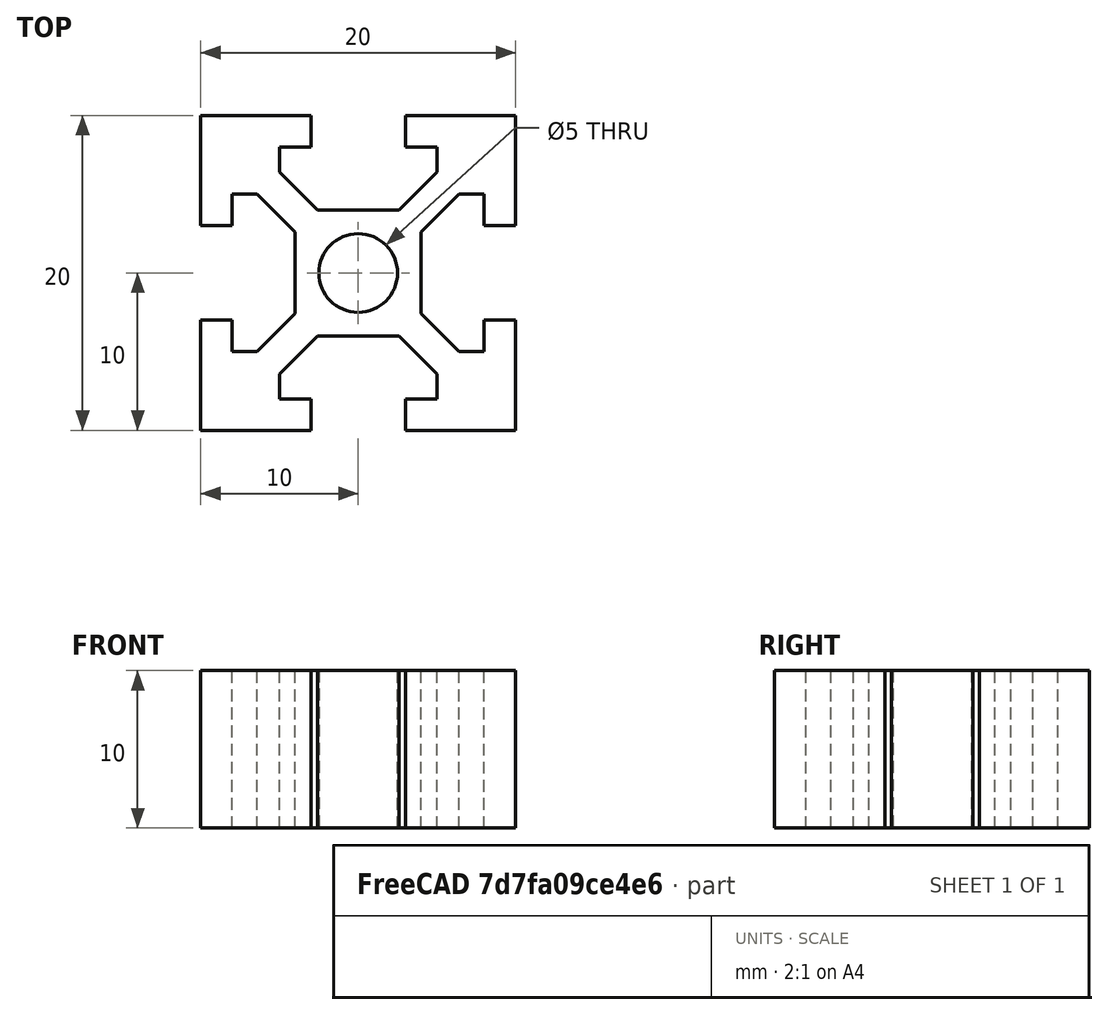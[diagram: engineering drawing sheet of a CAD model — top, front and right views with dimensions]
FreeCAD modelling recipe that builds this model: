
FCSTD DOCUMENT  (FreeCAD 0.19R24276 (Git))
Label: AL_profil_20
License: All rights reserved
LicenseURL: http://en.wikipedia.org/wiki/All_rights_reserved
objects: Sketcher::SketchObject×1, PartDesign::Pad×1, PartDesign::Body×1
note: 4 computed .brp shape members not serialized (recipe doc carries the construction recipe); baked Part::Feature solids carry a one-line shape summary decoded from their .brp

FEATURE [Sketcher::SketchObject] Sketch
  FullyConstrained = false
  MapMode = 5
  Support = -> [XY_Plane]
  sketch-geometry (106):
    g0: LineSegment StartX=10 StartY=10 StartZ=0 EndX=-10 EndY=10 EndZ=0
    g1: LineSegment StartX=-10 StartY=10 StartZ=0 EndX=-10 EndY=-10 EndZ=0
    g2: LineSegment StartX=-10 StartY=-10 StartZ=0 EndX=10 EndY=-10 EndZ=0
    g3: LineSegment StartX=10 StartY=-10 StartZ=0 EndX=10 EndY=10 EndZ=0
    g4: Circle CenterX=0 CenterY=0 CenterZ=0 NormalX=0 NormalY=0 NormalZ=1 AngleXU=0 Radius=14.1421
    g5: LineSegment StartX=4 StartY=4 StartZ=0 EndX=-4 EndY=4 EndZ=0
    g6: LineSegment StartX=-4 StartY=4 StartZ=0 EndX=-4 EndY=-4 EndZ=0
    g7: LineSegment StartX=-4 StartY=-4 StartZ=0 EndX=4 EndY=-4 EndZ=0
    g8: LineSegment StartX=4 StartY=-4 StartZ=0 EndX=4 EndY=4 EndZ=0
    g9: Circle CenterX=0 CenterY=0 CenterZ=0 NormalX=0 NormalY=0 NormalZ=1 AngleXU=0 Radius=5.65685
    g10: Circle CenterX=0 CenterY=0 CenterZ=0 NormalX=0 NormalY=0 NormalZ=1 AngleXU=0 Radius=2.5
    g11: LineSegment StartX=-10 StartY=-10 StartZ=0 EndX=-5 EndY=-10 EndZ=0
    g12: LineSegment StartX=-5 StartY=-10 StartZ=0 EndX=-5 EndY=-5 EndZ=0
    g13: LineSegment StartX=-5 StartY=-5 StartZ=0 EndX=-10 EndY=-5 EndZ=0
    g14: LineSegment StartX=-10 StartY=-5 StartZ=0 EndX=-10 EndY=-10 EndZ=0
    g15: LineSegment StartX=10 StartY=-10 StartZ=0 EndX=5 EndY=-10 EndZ=0
    g16: LineSegment StartX=5 StartY=-8 StartZ=0 EndX=5 EndY=-5 EndZ=0
    g17: LineSegment StartX=5 StartY=-5 StartZ=0 EndX=10 EndY=-5 EndZ=0
    g18: LineSegment StartX=10 StartY=-5 StartZ=0 EndX=10 EndY=-10 EndZ=0
    g19: LineSegment StartX=10 StartY=10 StartZ=0 EndX=5 EndY=10 EndZ=0
    g20: LineSegment StartX=5 StartY=10 StartZ=0 EndX=5 EndY=5 EndZ=0
    g21: LineSegment StartX=5 StartY=5 StartZ=0 EndX=10 EndY=5 EndZ=0
    g22: LineSegment StartX=10 StartY=5 StartZ=0 EndX=10 EndY=10 EndZ=0
    g23: LineSegment StartX=-10 StartY=10 StartZ=0 EndX=-5 EndY=10 EndZ=0
    g24: LineSegment StartX=-5 StartY=10 StartZ=0 EndX=-5 EndY=5 EndZ=0
    g25: LineSegment StartX=-5 StartY=5 StartZ=0 EndX=-10 EndY=5 EndZ=0
    g26: LineSegment StartX=-10 StartY=5 StartZ=0 EndX=-10 EndY=10 EndZ=0
    g27: LineSegment StartX=-6.41421 StartY=-5 StartZ=0 EndX=-4 EndY=-2.58579 EndZ=0
    g28: LineSegment StartX=-5 StartY=-6.41421 StartZ=0 EndX=-2.58579 EndY=-4 EndZ=0
    g29: LineSegment StartX=-5 StartY=-5 StartZ=0 EndX=-4 EndY=-4 EndZ=0
    g30: LineSegment StartX=-4 StartY=-4 StartZ=0 EndX=-5.70711 EndY=-5.70711 EndZ=0
    g31: LineSegment StartX=-6.41421 StartY=5 StartZ=0 EndX=-4 EndY=2.58579 EndZ=0
    g32: LineSegment StartX=-5 StartY=6.41421 StartZ=0 EndX=-2.58579 EndY=4 EndZ=0
    g33: LineSegment StartX=-5 StartY=5 StartZ=0 EndX=-4 EndY=4 EndZ=0
    g34: LineSegment StartX=-4 StartY=4 StartZ=0 EndX=-5.70711 EndY=5.70711 EndZ=0
    g35: LineSegment StartX=6.41421 StartY=-5 StartZ=0 EndX=4 EndY=-2.58579 EndZ=0
    g36: LineSegment StartX=5 StartY=-6.41421 StartZ=0 EndX=2.58579 EndY=-4 EndZ=0
    g37: LineSegment StartX=5 StartY=-5 StartZ=0 EndX=4 EndY=-4 EndZ=0
    g38: LineSegment StartX=4 StartY=-4 StartZ=0 EndX=5.70711 EndY=-5.70711 EndZ=0
    g39: LineSegment StartX=6.41421 StartY=5 StartZ=0 EndX=4 EndY=2.58579 EndZ=0
    g40: LineSegment StartX=5 StartY=6.41421 StartZ=0 EndX=2.58579 EndY=4 EndZ=0
    g41: LineSegment StartX=5 StartY=5 StartZ=0 EndX=4 EndY=4 EndZ=0
    g42: LineSegment StartX=4 StartY=4 StartZ=0 EndX=5.70711 EndY=5.70711 EndZ=0
    g43: LineSegment StartX=10 StartY=-10 StartZ=0 EndX=3 EndY=-10 EndZ=0
    g44: LineSegment StartX=3 StartY=-10 StartZ=0 EndX=3 EndY=-8 EndZ=0
    g45: LineSegment StartX=3 StartY=-8 StartZ=0 EndX=5 EndY=-8 EndZ=0
    g46: LineSegment StartX=10 StartY=-8 StartZ=0 EndX=10 EndY=-10 EndZ=0
    g47: LineSegment StartX=10 StartY=-3 StartZ=0 EndX=8 EndY=-3 EndZ=0
    g48: LineSegment StartX=8 StartY=-3 StartZ=0 EndX=8 EndY=-5 EndZ=0
    g49: LineSegment StartX=3 StartY=-10 StartZ=0 EndX=3 EndY=-8 EndZ=0
    g50: LineSegment StartX=3 StartY=-8 StartZ=0 EndX=5 EndY=-8 EndZ=0
    g51: LineSegment StartX=5 StartY=-8 StartZ=0 EndX=5 EndY=-6.41421 EndZ=0
    g52: LineSegment StartX=5 StartY=-6.41421 StartZ=0 EndX=2.58579 EndY=-4 EndZ=0
    g53: LineSegment StartX=4 StartY=-2.58579 StartZ=0 EndX=6.41421 EndY=-5 EndZ=0
    g54: LineSegment StartX=6.41421 StartY=-5 StartZ=0 EndX=8 EndY=-5 EndZ=0
    g55: LineSegment StartX=8 StartY=-5 StartZ=0 EndX=8 EndY=-3 EndZ=0
    g56: LineSegment StartX=8 StartY=-3 StartZ=0 EndX=10 EndY=-3 EndZ=0
    g57: LineSegment StartX=-2.58579 StartY=-4 StartZ=0 EndX=2.58579 EndY=-4 EndZ=0
    g58: LineSegment StartX=3 StartY=10 StartZ=0 EndX=3 EndY=8 EndZ=0
    g59: LineSegment StartX=3 StartY=8 StartZ=0 EndX=5 EndY=8 EndZ=0
    g60: LineSegment StartX=3 StartY=10 StartZ=0 EndX=3 EndY=8 EndZ=0
    g61: LineSegment StartX=3 StartY=8 StartZ=0 EndX=5 EndY=8 EndZ=0
    g62: LineSegment StartX=10 StartY=3 StartZ=0 EndX=8 EndY=3 EndZ=0
    g63: LineSegment StartX=8 StartY=3 StartZ=0 EndX=8 EndY=5 EndZ=0
    g64: LineSegment StartX=8 StartY=5 StartZ=0 EndX=8 EndY=3 EndZ=0
    g65: LineSegment StartX=8 StartY=3 StartZ=0 EndX=10 EndY=3 EndZ=0
    g66: LineSegment StartX=2.58579 StartY=4 StartZ=0 EndX=5 EndY=6.41421 EndZ=0
    g67: LineSegment StartX=5 StartY=6.41421 StartZ=0 EndX=5 EndY=8 EndZ=0
    g68: LineSegment StartX=-2.58579 StartY=4 StartZ=0 EndX=2.58579 EndY=4 EndZ=0
    g69: LineSegment StartX=4 StartY=2.58579 StartZ=0 EndX=6.41421 EndY=5 EndZ=0
    g70: LineSegment StartX=6.41421 StartY=5 StartZ=0 EndX=8 EndY=5 EndZ=0
    g71: LineSegment StartX=4 StartY=-2.58579 StartZ=0 EndX=4 EndY=2.58579 EndZ=0
    g72: LineSegment StartX=10 StartY=3 StartZ=0 EndX=10 EndY=10 EndZ=0
    g73: LineSegment StartX=10 StartY=-10 StartZ=0 EndX=10 EndY=-3 EndZ=0
    g74: LineSegment StartX=-3 StartY=-10 StartZ=0 EndX=-3 EndY=-8 EndZ=0
    g75: LineSegment StartX=-3 StartY=-8 StartZ=0 EndX=-5 EndY=-8 EndZ=0
    g76: LineSegment StartX=-3 StartY=-10 StartZ=0 EndX=-3 EndY=-8 EndZ=0
    g77: LineSegment StartX=-3 StartY=-8 StartZ=0 EndX=-5 EndY=-8 EndZ=0
    g78: LineSegment StartX=-5 StartY=-8 StartZ=0 EndX=-5 EndY=-6.41421 EndZ=0
    g79: LineSegment StartX=-10 StartY=-3 StartZ=0 EndX=-8 EndY=-3 EndZ=0
    g80: LineSegment StartX=-8 StartY=-3 StartZ=0 EndX=-8 EndY=-5 EndZ=0
    g81: LineSegment StartX=-6.41421 StartY=-5 StartZ=0 EndX=-8 EndY=-5 EndZ=0
    g82: LineSegment StartX=-8 StartY=-5 StartZ=0 EndX=-8 EndY=-3 EndZ=0
    g83: LineSegment StartX=-8 StartY=-3 StartZ=0 EndX=-10 EndY=-3 EndZ=0
    g84: LineSegment StartX=-10 StartY=10 StartZ=0 EndX=10 EndY=10 EndZ=0
    g85: LineSegment StartX=-6.41421 StartY=-5 StartZ=0 EndX=-4 EndY=-2.58579 EndZ=0
    g86: LineSegment StartX=-4 StartY=2.58579 StartZ=0 EndX=-4 EndY=-2.58579 EndZ=0
    g87: LineSegment StartX=-5 StartY=-6.41421 StartZ=0 EndX=-2.58579 EndY=-4 EndZ=0
    g88: LineSegment StartX=3 StartY=-10 StartZ=0 EndX=10 EndY=-10 EndZ=0
    g89: LineSegment StartX=-3 StartY=-10 StartZ=0 EndX=-10 EndY=-10 EndZ=0
    g90: LineSegment StartX=-10 StartY=3 StartZ=0 EndX=-8 EndY=3 EndZ=0
    g91: LineSegment StartX=-8 StartY=3 StartZ=0 EndX=-8 EndY=5 EndZ=0
    g92: LineSegment StartX=-8 StartY=5 StartZ=0 EndX=-8 EndY=3 EndZ=0
    g93: LineSegment StartX=-8 StartY=3 StartZ=0 EndX=-10 EndY=3 EndZ=0
    g94: LineSegment StartX=-3 StartY=10 StartZ=0 EndX=-3 EndY=8 EndZ=0
    g95: LineSegment StartX=-3 StartY=8 StartZ=0 EndX=-5 EndY=8 EndZ=0
    g96: LineSegment StartX=-3 StartY=10 StartZ=0 EndX=-3 EndY=8 EndZ=0
    g97: LineSegment StartX=-3 StartY=8 StartZ=0 EndX=-5 EndY=8 EndZ=0
    g98: LineSegment StartX=-5 StartY=8 StartZ=0 EndX=-5 EndY=6.41421 EndZ=0
    g99: LineSegment StartX=-6.41421 StartY=5 StartZ=0 EndX=-8 EndY=5 EndZ=0
    g100: LineSegment StartX=-5 StartY=6.41421 StartZ=0 EndX=-2.58579 EndY=4 EndZ=0
    g101: LineSegment StartX=-6.41421 StartY=5 StartZ=0 EndX=-4 EndY=2.58579 EndZ=0
    g102: LineSegment StartX=-10 StartY=-3 StartZ=0 EndX=-10 EndY=-10 EndZ=0
    g103: LineSegment StartX=-10 StartY=3 StartZ=0 EndX=-10 EndY=10 EndZ=0
    g104: LineSegment StartX=-10 StartY=10 StartZ=0 EndX=-3 EndY=10 EndZ=0
    g105: LineSegment StartX=3 StartY=10 StartZ=0 EndX=10 EndY=10 EndZ=0
  constraints (271):
    c: Coincident(g0,g1)
    c: Coincident(g1,g2)
    c: Coincident(g2,g3)
    c: Coincident(g3,g0)
    c: Equal(g0,g1)
    c: Equal(g0,g2)
    c: Equal(g0,g3)
    c: PointOnObject(g0,g4)
    c: PointOnObject(g1,g4)
    c: PointOnObject(g2,g4)
    c: PointOnObject(g3,g4)
    c: Coincident(g4,g-1)
    c: Horizontal(g0)
    c: Coincident(g5,g6)
    c: Coincident(g6,g7)
    c: Coincident(g7,g8)
    c: Coincident(g8,g5)
    c: Equal(g5,g6)
    c: Equal(g5,g7)
    c: Equal(g5,g8)
    c: PointOnObject(g5,g9)
    c: PointOnObject(g6,g9)
    c: PointOnObject(g7,g9)
    c: PointOnObject(g8,g9)
    c: Coincident(g9,g-1)
    c: Horizontal(g5)
    c: DistanceX(g5,g5) = 8
    c: Diameter(g10) = 5
    c: DistanceX(g2,g2) = 20
    c: Coincident(g10,g-1)
    c: Coincident(g11,g12)
    c: Coincident(g12,g13)
    c: Coincident(g13,g14)
    c: Coincident(g14,g11)
    c: Horizontal(g11)
    c: Horizontal(g13)
    c: Vertical(g12)
    c: Vertical(g14)
    c: Coincident(g11,g1)
    c: Coincident(g16,g17)
    c: Coincident(g17,g18)
    c: Coincident(g18,g15)
    c: Horizontal(g15)
    c: Horizontal(g17)
    c: Vertical(g16)
    c: Vertical(g18)
    c: Coincident(g15,g2)
    c: Coincident(g19,g20)
    c: Coincident(g20,g21)
    c: Coincident(g21,g22)
    c: Coincident(g22,g19)
    c: Horizontal(g19)
    c: Horizontal(g21)
    c: Vertical(g20)
    c: Vertical(g22)
    c: Coincident(g19,g0)
    c: Coincident(g23,g24)
    c: Coincident(g24,g25)
    c: Coincident(g25,g26)
    c: Coincident(g26,g23)
    c: Horizontal(g23)
    c: Horizontal(g25)
    c: Vertical(g24)
    c: Vertical(g26)
    c: Coincident(g23,g0)
    c: DistanceX(g1,g11) = 5
    c: Equal(g12,g13)
    c: Equal(g13,g17)
    c: Equal(g25,g13)
    c: Equal(g13,g21)
    c: Equal(g24,g20)
    c: Equal(g20,g12)
    c: Parallel(g27,g28)
    c: Coincident(g29,g12)
    c: Coincident(g29,g6)
    c: Parallel(g27,g29)
    c: Coincident(g30,g6)
    c: Parallel(g29,g30)
    c: PointOnObject(g28,g12)
    c: PointOnObject(g27,g13)
    c: Distance(g28,g27) = 2
    c: PointOnObject(g27,g6)
    c: PointOnObject(g28,g7)
    c: Symmetric(g27,g28,g30)
    c: Parallel(g31,g32)
    c: Parallel(g31,g33)
    c: Parallel(g33,g34)
    c: Coincident(g33,g34)
    c: Coincident(g33,g5)
    c: Coincident(g33,g24)
    c: PointOnObject(g31,g25)
    c: PointOnObject(g32,g24)
    c: PointOnObject(g32,g5)
    c: PointOnObject(g31,g6)
    c: Symmetric(g31,g32,g34)
    c: Distance(g31,g32) = 2
    c: Parallel(g35,g36)
    c: Parallel(g35,g37)
    c: Parallel(g37,g38)
    c: Parallel(g39,g40)
    c: Parallel(g39,g41)
    c: Parallel(g41,g42)
    c: Coincident(g41,g42)
    c: Coincident(g41,g5)
    c: PointOnObject(g40,g5)
    c: PointOnObject(g39,g8)
    c: PointOnObject(g39,g21)
    c: PointOnObject(g40,g20)
    c: Coincident(g20,g41)
    c: Distance(g40,g39) = 2
    c: Symmetric(g40,g39,g42)
    c: PointOnObject(g35,g8)
    c: PointOnObject(g35,g17)
    c: PointOnObject(g36,g16)
    c: PointOnObject(g36,g7)
    c: Coincident(g38,g37)
    c: Coincident(g38,g7)
    c: Coincident(g37,g16)
    c: Symmetric(g36,g35,g38)
    c: Distance(g36,g35) = 2
    c: Coincident(g43,g44)
    c: Coincident(g44,g45)
    c: Coincident(g46,g43)
    c: Horizontal(g43)
    c: Horizontal(g45)
    c: Vertical(g44)
    c: Vertical(g46)
    c: Coincident(g43,g2)
    c: DistanceX(g43,g2) = 7
    c: DistanceY(g2,g46) = 2
    c: Coincident(g45,g16)
    c: Coincident(g47,g48)
    c: Equal(g44,g47)
    c: Vertical(g48)
    c: Horizontal(g47)
    c: Vertical(g47,g2)
    c: Horizontal(g17,g13)
    c: PointOnObject(g48,g17)
    c: DistanceY(g2,g47) = 7
    c: DistanceX(g47,g47) = 2
    c: Coincident(g49,g43)
    c: Coincident(g50,g44)
    c: Coincident(g51,g50)
    c: Coincident(g52,g51)
    c: Coincident(g53,g35)
    c: Coincident(g54,g53)
    c: Coincident(g55,g48)
    c: Coincident(g56,g55)
    c: Coincident(g49,g50)
    c: Coincident(g50,g16)
    c: Coincident(g51,g36)
    c: Coincident(g52,g36)
    c: Coincident(g53,g35)
    c: Coincident(g54,g55)
    c: Coincident(g55,g47)
    c: Coincident(g56,g47)
    c: Coincident(g57,g28)
    c: Coincident(g57,g52)
    c: Coincident(g58,g59)
    c: Horizontal(g59)
    c: Vertical(g58)
    c: Coincident(g62,g63)
    c: Equal(g58,g62)
    c: Vertical(g63)
    c: Horizontal(g62)
    c: Coincident(g61,g58)
    c: Coincident(g64,g63)
    c: Coincident(g65,g64)
    c: Coincident(g60,g61)
    c: Coincident(g64,g62)
    c: Coincident(g65,g62)
    c: Equal(g56,g65)
    c: Vertical(g65,g56)
    c: Equal(g55,g64)
    c: Horizontal(g64,g21)
    c: Equal(g61,g64)
    c: Horizontal(g60,g19)
    c: Coincident(g60,g58)
    c: Coincident(g61,g59)
    c: Vertical(g61,g19)
    c: Coincident(g66,g40)
    c: Coincident(g67,g66)
    c: Coincident(g67,g61)
    c: Coincident(g66,g40)
    c: Coincident(g68,g32)
    c: Coincident(g68,g66)
    c: Coincident(g69,g39)
    c: Coincident(g70,g69)
    c: Coincident(g69,g39)
    c: Coincident(g70,g64)
    c: Coincident(g71,g53)
    c: Coincident(g71,g69)
    c: Coincident(g72,g65)
    c: Coincident(g72,g0)
    c: Coincident(g73,g2)
    c: Coincident(g73,g56)
    c: Horizontal(g84)
    c: Coincident(g74,g75)
    c: Horizontal(g75)
    c: Vertical(g74)
    c: Coincident(g79,g80)
    c: Equal(g74,g79)
    c: Vertical(g80)
    c: Horizontal(g79)
    c: Coincident(g77,g74)
    c: Coincident(g78,g77)
    c: Coincident(g82,g80)
    c: Coincident(g83,g82)
    c: Coincident(g76,g77)
    c: Coincident(g81,g82)
    c: Coincident(g82,g79)
    c: Coincident(g83,g79)
    c: Horizontal(g76,g49)
    c: Horizontal(g76,g49)
    c: Vertical(g78)
    c: Coincident(g77,g75)
    c: Coincident(g78,g28)
    c: Equal(g77,g50)
    c: Vertical(g83,g1)
    c: Coincident(g74,g76)
    c: Equal(g82,g77)
    c: Horizontal(g81)
    c: Coincident(g81,g27)
    c: Coincident(g85,g81)
    c: Coincident(g85,g27)
    c: Coincident(g86,g31)
    c: Coincident(g86,g85)
    c: Coincident(g87,g78)
    c: Coincident(g87,g57)
    c: Coincident(g88,g49)
    c: Coincident(g89,g76)
    c: Coincident(g1,g89)
    c: Coincident(g88,g73)
    c: Coincident(g94,g95)
    c: Horizontal(g95)
    c: Vertical(g94)
    c: Coincident(g90,g91)
    c: Equal(g94,g90)
    c: Vertical(g91)
    c: Horizontal(g90)
    c: Coincident(g97,g94)
    c: Coincident(g98,g97)
    c: Coincident(g92,g91)
    c: Coincident(g93,g92)
    c: Coincident(g96,g97)
    c: Coincident(g99,g92)
    c: Coincident(g92,g90)
    c: Coincident(g93,g90)
    c: Vertical(g98)
    c: Coincident(g97,g95)
    c: Coincident(g94,g96)
    c: Equal(g92,g97)
    c: Horizontal(g99)
    c: Horizontal(g96,g23)
    c: Equal(g97,g61)
    c: Horizontal(g60,g96)
    c: Coincident(g98,g32)
    c: Coincident(g100,g98)
    c: Coincident(g68,g100)
    c: Coincident(g99,g31)
    c: Vertical(g92,g82)
    c: Coincident(g101,g99)
    c: Coincident(g101,g86)
    c: Coincident(g102,g83)
    c: Coincident(g103,g93)
    c: Coincident(g104,g0)
    c: Coincident(g105,g60)
    c: Coincident(g103,g104)
    c: Coincident(g102,g89)
    c: Coincident(g104,g96)
    c: Coincident(g105,g72)
FEATURE [PartDesign::Pad] Pad
  Direction = (1,1,1)
  Length = 10
  Length2 = 100
  Profile = -> Sketch
  Type = 0
FEATURE [PartDesign::Body] Body
  Group = -> [Sketch,Pad]
  Origin = -> Origin
  Tip = -> Pad
